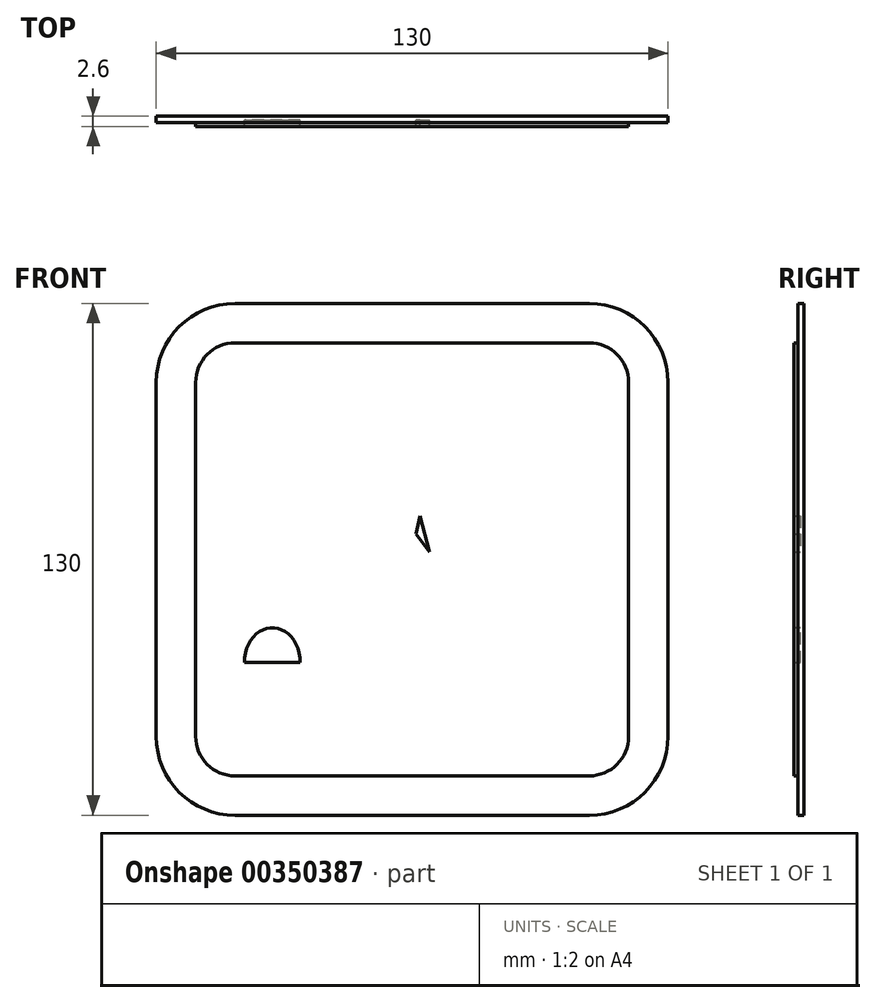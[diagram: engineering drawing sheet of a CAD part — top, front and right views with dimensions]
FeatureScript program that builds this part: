
annotation { "Feature Type Name" : "Feature", "Feature Type Description" : "" }
export const myFeature = defineFeature(function(context is Context, id is Id, definition is map)
    precondition{}
    {
        {
            var Q0;
            Q0=qCreatedBy(makeId("Front.planeOp"),FACE);
            var sketch = newSketch(context, id + "F0", { "sketchPlane" : qUnion([Q0])});
            skLineSegment(sketch, "E0.bottom", {"start": v(20, 0) * mm, "end": v(65, 0) * mm});
            skLineSegment(sketch, "E0.top", {"start": v(20, 130) * mm, "end": v(65, 130) * mm});
            skLineSegment(sketch, "E0.left", {"start": v(0, 20) * mm, "end": v(0, 110) * mm});
            skArc(sketch, "E1", {"start": v(0, 20) * mm, "mid": v(5.86, 5.86) * mm, "end": v(20, 0) * mm});
            skArc(sketch, "E2", {"start": v(20, 130) * mm, "mid": v(5.86, 124.14) * mm, "end": v(0, 110) * mm});
            skPoint(sketch, "E3.orphan", {"position": v(0, 130) * mm});
            skPoint(sketch, "E4.orphan", {"position": v(0, 0) * mm});
            skArc(sketch, "E5.MirrorCS", {"start": v(110, 130) * mm, "mid": v(124.14, 124.14) * mm, "end": v(130, 110) * mm});
            skLineSegment(sketch, "E6.MirrorCS", {"start": v(110, 130) * mm, "end": v(65, 130) * mm});
            skLineSegment(sketch, "E7.MirrorCS", {"start": v(130, 20) * mm, "end": v(130, 110) * mm});
            skArc(sketch, "E8.MirrorCS", {"start": v(130, 20) * mm, "mid": v(124.14, 5.86) * mm, "end": v(110, 0) * mm});
            skLineSegment(sketch, "E9.MirrorCS", {"start": v(110, 0) * mm, "end": v(65, 0) * mm});
            skLineSegment(sketch, "E10.0", {"start": v(110, 120) * mm, "end": v(65, 120) * mm});
            skLineSegment(sketch, "E10.1", {"start": v(20, 120) * mm, "end": v(65, 120) * mm});
            skArc(sketch, "E10.2", {"start": v(110, 120) * mm, "mid": v(117.07, 117.07) * mm, "end": v(120, 110) * mm});
            skArc(sketch, "E10.3", {"start": v(20, 120) * mm, "mid": v(12.93, 117.07) * mm, "end": v(10, 110) * mm});
            skLineSegment(sketch, "E10.4", {"start": v(10, 20) * mm, "end": v(10, 110) * mm});
            skArc(sketch, "E10.5", {"start": v(10, 20) * mm, "mid": v(12.93, 12.93) * mm, "end": v(20, 10) * mm});
            skLineSegment(sketch, "E10.6", {"start": v(120, 20) * mm, "end": v(120, 110) * mm});
            skArc(sketch, "E10.7", {"start": v(120, 20) * mm, "mid": v(117.07, 12.93) * mm, "end": v(110, 10) * mm});
            skLineSegment(sketch, "E10.8", {"start": v(110, 10) * mm, "end": v(65, 10) * mm});
            skLineSegment(sketch, "E10.9", {"start": v(20, 10) * mm, "end": v(65, 10) * mm});
            skCircle(sketch, "E11", {"center": v(68.6, 104) * mm, "radius": 7.5 * mm});
            skArc(sketch, "E12", {"start": v(68.65, 21.84) * mm, "mid": v(74.16, 18.65) * mm, "end": v(77.35, 24.16) * mm});
            skArc(sketch, "E13", {"start": v(47.5, 23) * mm, "mid": v(52, 18.5) * mm, "end": v(56.5, 23) * mm});
            skArc(sketch, "E14", {"start": v(72.35, 59.73) * mm, "mid": v(72.9, 55.3) * mm, "end": v(77.02, 53.53) * mm});
            skLineSegment(sketch, "E15", {"start": v(80.85, 59.16) * mm, "end": v(73.22, 87.62) * mm});
            skLineSegment(sketch, "E16", {"start": v(47.5, 66) * mm, "end": v(47.5, 23) * mm});
            skLineSegment(sketch, "E17", {"start": v(56.5, 23) * mm, "end": v(56.5, 55) * mm});
            skLineSegment(sketch, "E18", {"start": v(59.66, 55.42) * mm, "end": v(68.65, 21.84) * mm});
            skLineSegment(sketch, "E19", {"start": v(77.35, 24.16) * mm, "end": v(65.32, 69.07) * mm});
            skLineSegment(sketch, "E20", {"start": v(60.6, 96) * mm, "end": v(65.49, 94.96) * mm});
            skArc(sketch, "E21", {"start": v(60.6, 96) * mm, "mid": v(55.22, 95.69) * mm, "end": v(50.76, 92.69) * mm});
            skArc(sketch, "E22", {"start": v(73.22, 87.62) * mm, "mid": v(70.39, 92.38) * mm, "end": v(65.49, 94.96) * mm});
            skLineSegment(sketch, "E23", {"start": v(39.5, 38.8) * mm, "end": v(39.12, 35.8) * mm});
            skLineSegment(sketch, "E24", {"start": v(37, 18.5) * mm, "end": v(22, 18.5) * mm});
            skLineSegment(sketch, "E25", {"start": v(22, 18.5) * mm, "end": v(20.06, 34.3) * mm});
            skLineSegment(sketch, "E26", {"start": v(19.5, 38.8) * mm, "end": v(39.5, 38.8) * mm});
            skEllipticalArc(sketch, "E27", {});
            skFitSpline(sketch, "E28.0", {"points": [v(30.32, 48.61) * mm, v(29.5, 48.66) * mm, v(28.68, 48.61) * mm, v(27.6, 48.41) * mm, v(26.57, 48.02) * mm, v(25.6, 47.45) * mm, v(24.68, 46.76) * mm, v(23.67, 45.72) * mm, v(22.85, 44.47) * mm, v(22.31, 43.37) * mm, v(21.88, 42.21) * mm, v(21.58, 41) * mm, v(21.43, 39.75) * mm, v(21.4, 38.8) * mm, v(21.43, 37.85) * mm, v(21.58, 36.6) * mm, v(21.88, 35.39) * mm, v(22.31, 34.23) * mm, v(22.85, 33.13) * mm, v(23.67, 31.88) * mm, v(24.68, 30.84) * mm, v(25.6, 30.15) * mm, v(26.57, 29.58) * mm, v(27.6, 29.19) * mm, v(28.68, 28.99) * mm, v(29.5, 28.94) * mm, v(30.32, 28.99) * mm, v(31.4, 29.19) * mm, v(32.43, 29.58) * mm, v(33.4, 30.15) * mm, v(34.32, 30.84) * mm, v(35.33, 31.88) * mm, v(36.15, 33.13) * mm, v(36.69, 34.23) * mm, v(37.12, 35.39) * mm, v(37.42, 36.6) * mm, v(37.57, 37.85) * mm, v(37.6, 38.8) * mm, v(37.57, 39.75) * mm, v(37.42, 41) * mm, v(37.12, 42.21) * mm, v(36.69, 43.37) * mm, v(36.15, 44.47) * mm, v(35.33, 45.72) * mm, v(34.32, 46.76) * mm, v(33.4, 47.45) * mm, v(32.43, 48.02) * mm, v(31.4, 48.41) * mm, v(30.32, 48.61) * mm, v(29.5, 48.66) * mm, v(28.68, 48.61) * mm]});
            skPoint(sketch, "E29.endSnap0", {"position": v(29.5, 47.65) * mm});
            skLineSegment(sketch, "E30.bottom", {"start": v(19.88, 35.8) * mm, "end": v(39.12, 35.8) * mm});
            skLineSegment(sketch, "E31.trimOffspring", {"start": v(19.88, 35.8) * mm, "end": v(19.5, 38.8) * mm});
            skLineSegment(sketch, "E32.trimOffspring", {"start": v(38.94, 34.3) * mm, "end": v(37, 18.5) * mm});
            skLineSegment(sketch, "E33", {"start": v(20.06, 34.3) * mm, "end": v(38.94, 34.3) * mm});
            skLineSegment(sketch, "E34", {"start": v(65.32, 69.07) * mm, "end": v(72.35, 59.73) * mm});
            skLineSegment(sketch, "E35", {"start": v(95, 18.5) * mm, "end": v(105, 18.5) * mm});
            skLineSegment(sketch, "E36", {"start": v(107, 20.5) * mm, "end": v(107, 20.5) * mm});
            skLineSegment(sketch, "E37", {"start": v(105, 22.5) * mm, "end": v(95, 22.5) * mm});
            skLineSegment(sketch, "E38", {"start": v(93, 20.5) * mm, "end": v(93, 20.5) * mm});
            skArc(sketch, "E39", {"start": v(96.78, 32.3) * mm, "mid": v(95.97, 32.93) * mm, "end": v(94.94, 33.07) * mm});
            skArc(sketch, "E40", {"start": v(98.4, 23.5) * mm, "mid": v(101.2, 23.1) * mm, "end": v(101.6, 25.9) * mm});
            skLineSegment(sketch, "E41", {"start": v(96.78, 32.3) * mm, "end": v(101.6, 25.9) * mm});
            skLineSegment(sketch, "E42", {"start": v(93.59, 29.89) * mm, "end": v(98.4, 23.5) * mm});
            skArc(sketch, "E43.trimOffspring", {"start": v(93.34, 31.87) * mm, "mid": v(93.2, 30.85) * mm, "end": v(93.59, 29.89) * mm});
            skPoint(sketch, "E44.visualSharp", {"position": v(93, 22.5) * mm});
            skArc(sketch, "E44.filletArc", {"start": v(95, 22.5) * mm, "mid": v(93.59, 21.91) * mm, "end": v(93, 20.5) * mm});
            skPoint(sketch, "E45.visualSharp", {"position": v(93, 18.5) * mm});
            skArc(sketch, "E45.filletArc", {"start": v(93, 20.5) * mm, "mid": v(93.59, 19.09) * mm, "end": v(95, 18.5) * mm});
            skPoint(sketch, "E46.visualSharp", {"position": v(107, 22.5) * mm});
            skArc(sketch, "E46.filletArc", {"start": v(107, 20.5) * mm, "mid": v(106.41, 21.91) * mm, "end": v(105, 22.5) * mm});
            skPoint(sketch, "E47.visualSharp", {"position": v(107, 18.5) * mm});
            skArc(sketch, "E47.filletArc", {"start": v(105, 18.5) * mm, "mid": v(106.41, 19.09) * mm, "end": v(107, 20.5) * mm});
            skLineSegment(sketch, "E48", {"start": v(47.5, 66) * mm, "end": v(49.08, 73.42) * mm});
            skLineSegment(sketch, "E49.trimOffspring", {"start": v(78.99, 54.25) * mm, "end": v(94.94, 33.07) * mm});
            skLineSegment(sketch, "E50.trimOffspring", {"start": v(77.02, 53.53) * mm, "end": v(93.34, 31.87) * mm});
            skArc(sketch, "E51.trimOffspring", {"start": v(78.99, 54.25) * mm, "mid": v(80.7, 56.4) * mm, "end": v(80.85, 59.16) * mm});
            skArc(sketch, "E52", {"start": v(59.66, 55.42) * mm, "mid": v(57.9, 56.6) * mm, "end": v(56.5, 55) * mm});
            skLineSegment(sketch, "E53", {"start": v(67.01, 76.03) * mm, "end": v(69.46, 66.9) * mm});
            skLineSegment(sketch, "E54", {"start": v(67.01, 76.03) * mm, "end": v(66.03, 71.43) * mm});
            skLineSegment(sketch, "E55", {"start": v(66.03, 71.43) * mm, "end": v(69.46, 66.9) * mm});
            skPoint(sketch, "E56.orphan", {"position": v(65.32, 69.07) * mm});
            skLineSegment(sketch, "E57", {"start": v(50.76, 92.69) * mm, "end": v(44.24, 85.13) * mm});
            skArc(sketch, "E58", {"start": v(56.6, 67.75) * mm, "mid": v(63.07, 73.83) * mm, "end": v(54.95, 70.25) * mm});
            skLineSegment(sketch, "E59", {"start": v(49.08, 73.42) * mm, "end": v(56.6, 67.75) * mm});
            skLineSegment(sketch, "E60.0", {"start": v(45.03, 77.73) * mm, "end": v(54.95, 70.25) * mm});
            skArc(sketch, "E61", {"start": v(44.24, 85.13) * mm, "mid": v(43.03, 81.26) * mm, "end": v(45.03, 77.73) * mm});
            skPoint(sketch, "E62.orphan", {"position": v(45.03, 77.73) * mm});
            const initialGuessF0  = {"E27": [0.0295, 0.0388, 0, 1, 0.008845195174217224, 0.007091434044851545, 4.71238898038469, 1.5707963267948966]};
            skSetInitialGuess(sketch, initialGuessF0);
            skSolve(sketch);
        }
        {
            var Q0;
            Q0=makeQuery(id+"F0.imprint","IMPRINT",FACE,{"disambiguationData":[TD([[makeQuery(id+"F0.imprint","IMPRINT",EDGE,{"derivedFrom":sQuery(id+"F0.wireOp",EDGE,"E0.bottom")}),1.0]])]});
            var Q1;
            Q1=makeQuery(id+"F0.imprint","IMPRINT",FACE,{"disambiguationData":[TD([[makeQuery(id+"F0.imprint","IMPRINT",EDGE,{"derivedFrom":sQuery(id+"F0.wireOp",EDGE,"E10.0")}),1.0]])]});
            var Q2;
            Q2=makeQuery(id+"F0.imprint","IMPRINT",FACE,{"disambiguationData":[TD([[makeQuery(id+"F0.imprint","IMPRINT",EDGE,{"derivedFrom":sQuery(id+"F0.wireOp",EDGE,"E24")}),-1.0]])]});
            var Q3;
            {var subQ0=sQuery(id+"F0.wireOp",EDGE,"E27");Q3=makeQuery(id+"F0.imprint","IMPRINT",FACE,{"disambiguationData":[TD([[makeQuery(id+"F0.imprint","IMPRINT",EDGE,{"derivedFrom":subQ0}),1.0]])]});}
            var Q4;
            Q4=makeQuery(id+"F0.imprint","IMPRINT",FACE,{"disambiguationData":[TD([[makeQuery(id+"F0.imprint","IMPRINT",EDGE,{"derivedFrom":sQuery(id+"F0.wireOp",EDGE,"E12")}),1.0]])]});
            var Q5;
            Q5=makeQuery(id+"F0.imprint","IMPRINT",FACE,{"disambiguationData":[TD([[makeQuery(id+"F0.imprint","IMPRINT",EDGE,{"derivedFrom":sQuery(id+"F0.wireOp",EDGE,"E11")}),1.0]])]});
            var Q6;
            Q6=makeQuery(id+"F0.imprint","IMPRINT",FACE,{"disambiguationData":[TD([[makeQuery(id+"F0.imprint","IMPRINT",EDGE,{"derivedFrom":sQuery(id+"F0.wireOp",EDGE,"VmvuncxO-awzD-P3L9-Sl9Z-NsoimtpyMnnJ")}),1.0]])]});
            var Q7;
            {var subQ1=sQuery(id+"F0.wireOp",EDGE,"CPTJZFOj-02Jz-4RJi-PxtP-rUuO0vZowl4J");Q7=makeQuery(id+"F0.imprint","IMPRINT",FACE,{"disambiguationData":[TD([[makeQuery(id+"F0.imprint","IMPRINT",EDGE,{"derivedFrom":subQ1}),-1.0]])]});}
            var Q8;
            Q8=makeQuery(id+"F0.imprint","IMPRINT",FACE,{"disambiguationData":[TD([[makeQuery(id+"F0.imprint","IMPRINT",EDGE,{"derivedFrom":sQuery(id+"F0.wireOp",EDGE,"E35")}),1.0]])]});
            var Q9;
            {var subQ7=sQuery(id+"F0.wireOp",EDGE,"E23");Q9=makeQuery(id+"F0.imprint","IMPRINT",FACE,{"disambiguationData":[TD([[makeQuery(id+"F0.imprint","IMPRINT",EDGE,{"derivedFrom":subQ7}),-1.0]])]});}
            var Q10;
            {var subQ0=sQuery(id+"F0.wireOp",EDGE,"E27");Q10=makeQuery(id+"F0.imprint","IMPRINT",FACE,{"disambiguationData":[TD([[makeQuery(id+"F0.imprint","IMPRINT",EDGE,{"derivedFrom":subQ0}),-1.0]])]});}
            var Q11;
            Q11=makeQuery(id+"F0.imprint","IMPRINT",FACE,{"disambiguationData":[TD([[makeQuery(id+"F0.imprint","IMPRINT",EDGE,{"derivedFrom":sQuery(id+"F0.wireOp",EDGE,"E53")}),-1.0]])]});
            var Q12;
            Q12=sQuery(id+"F0.wireOp",EDGE,"E8.MirrorCS");
            var Q13;
            Q13=sQuery(id+"F0.wireOp",EDGE,"E7.MirrorCS");
            var Q14;
            Q14=sQuery(id+"F0.wireOp",EDGE,"E5.MirrorCS");
            var Q15;
            Q15=sQuery(id+"F0.wireOp",EDGE,"E6.MirrorCS");
            var Q16;
            Q16=sQuery(id+"F0.wireOp",EDGE,"E0.top");
            var Q17;
            Q17=sQuery(id+"F0.wireOp",EDGE,"E2");
            var Q18;
            Q18=sQuery(id+"F0.wireOp",EDGE,"E0.left");
            var Q19;
            Q19=sQuery(id+"F0.wireOp",EDGE,"E1");
            var Q20;
            Q20=sQuery(id+"F0.wireOp",EDGE,"E0.bottom");
            var Q21;
            Q21=sQuery(id+"F0.wireOp",EDGE,"E9.MirrorCS");
            extrude(context, id + "F1", {"entities" : qUnion([Q0, Q1, Q2, Q3, Q4, Q5, Q6, Q7, Q8, Q9, Q10, Q11]), "surfaceEntities" : qUnion([Q12, Q13, Q14, Q15, Q16, Q17, Q18, Q19, Q20, Q21]), "oppositeDirection" : true, "depth" : 1 * mm});
        }
        {
            var Q0;
            Q0=makeQuery(id+"F0.imprint","IMPRINT",FACE,{"disambiguationData":[TD([[makeQuery(id+"F0.imprint","IMPRINT",EDGE,{"derivedFrom":sQuery(id+"F0.wireOp",EDGE,"E0.bottom")}),1.0]])]});
            extrude(context, id + "F2", {"entities" : qUnion([Q0]), "operationType" : NewBodyOperationType.ADD, "depth" : 0.6 * mm});
        }
        {
            var Q0;
            Q0=makeQuery(id+"F0.imprint","IMPRINT",FACE,{"disambiguationData":[TD([[makeQuery(id+"F0.imprint","IMPRINT",EDGE,{"derivedFrom":sQuery(id+"F0.wireOp",EDGE,"E12")}),1.0]])]});
            var Q1;
            {var subQ0=sQuery(id+"F0.wireOp",EDGE,"E27");Q1=makeQuery(id+"F0.imprint","IMPRINT",FACE,{"disambiguationData":[TD([[makeQuery(id+"F0.imprint","IMPRINT",EDGE,{"derivedFrom":subQ0}),-1.0]])]});}
            var Q2;
            {var subQ7=sQuery(id+"F0.wireOp",EDGE,"E23");Q2=makeQuery(id+"F0.imprint","IMPRINT",FACE,{"disambiguationData":[TD([[makeQuery(id+"F0.imprint","IMPRINT",EDGE,{"derivedFrom":subQ7}),-1.0]])]});}
            var Q3;
            Q3=makeQuery(id+"F0.imprint","IMPRINT",FACE,{"disambiguationData":[TD([[makeQuery(id+"F0.imprint","IMPRINT",EDGE,{"derivedFrom":sQuery(id+"F0.wireOp",EDGE,"E24")}),-1.0]])]});
            var Q4;
            Q4=makeQuery(id+"F0.imprint","IMPRINT",FACE,{"disambiguationData":[TD([[makeQuery(id+"F0.imprint","IMPRINT",EDGE,{"derivedFrom":sQuery(id+"F0.wireOp",EDGE,"E11")}),1.0]])]});
            var Q5;
            Q5=makeQuery(id+"F0.imprint","IMPRINT",FACE,{"disambiguationData":[TD([[makeQuery(id+"F0.imprint","IMPRINT",EDGE,{"derivedFrom":sQuery(id+"F0.wireOp",EDGE,"E35")}),1.0]])]});
            extrude(context, id + "F3", {"entities" : qUnion([Q0, Q1, Q2, Q3, Q4, Q5]), "operationType" : NewBodyOperationType.ADD, "depth" : 1.6 * mm});
        }
    });
